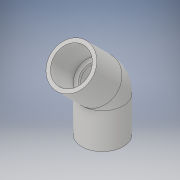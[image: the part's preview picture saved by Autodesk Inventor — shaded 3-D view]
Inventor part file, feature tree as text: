
AUTODESK INVENTOR PART (.ipt)
format: ipt  version: 2018.2 (Build 222227000, 227)  size: 172,032 bytes
history: native  units: in
note: dims shown in document units (in); Inventor stores cm internally (conversion verified against a paired STEP export)
features: sketch x10, extrude x6, plane x5, revolve x2, other x1
ambient origin geometry x8: Origin, YZ Plane, XZ Plane, XY Plane, X Axis, Y Axis, Z Axis, Center Point
bodies: Solid1 (feature_tree)
feature tree (24):
  extrude  "Extrusion1"  Depth=1.367in TaperAngle=0.0deg
  sketch  "Sketch2"  dims[d3=-0.3092in d4=1.367in d5=0.0in]
  plane  "Work Plane1"
  extrude  "Extrusion2"  Depth=1.367in TaperAngle=0.0deg
  extrude  "Extrusion3"  Depth=1.25in TaperAngle=0.0deg
  extrude  "Extrusion4"  Depth=1.25in TaperAngle=0.0deg
  plane  "Work Plane2"
  plane  "Work Plane3"
  revolve  "Revolution1"  Angle=45.0deg
  plane  "Work Plane4"
  sketch  "Sketch6"  dims[d15=-0.3092in d17=1.0in]
  plane  "Work Plane5"
  sketch  "Sketch8"  dims[d18=0.117in d19=0.0in d20=1.0in]
  extrude  "Extrusion5"  Depth=1.0in
  extrude  "Extrusion6"  Depth=1.0in
  other  "Work Axis1"
  revolve  "Revolution2"  [1 undecoded]
  sketch  "Sketch1"  dims[d0=1.605in d1=1.367in d2=0.0in]
  sketch  "Sketch3"  dims[d6=1.321in d7=1.25in d8=0.0in]
  sketch  "Sketch4"  dims[d9=1.321in d10=1.25in d11=0.0in]
  sketch  "Sketch5"  dims[d12=0.0in d13=0.0in d14=45.0deg]
  sketch  "Sketch9"  dims[d21=0.117in d22=0.0in d23=0.2749in]
  sketch  "Sketch10"
  sketch  "Sketch11"
note: 1 required parameter value undecoded (feature->parameter linkage not recoverable at this tier; creation-order binding heuristic only, values carry confidence <= 0.55)
